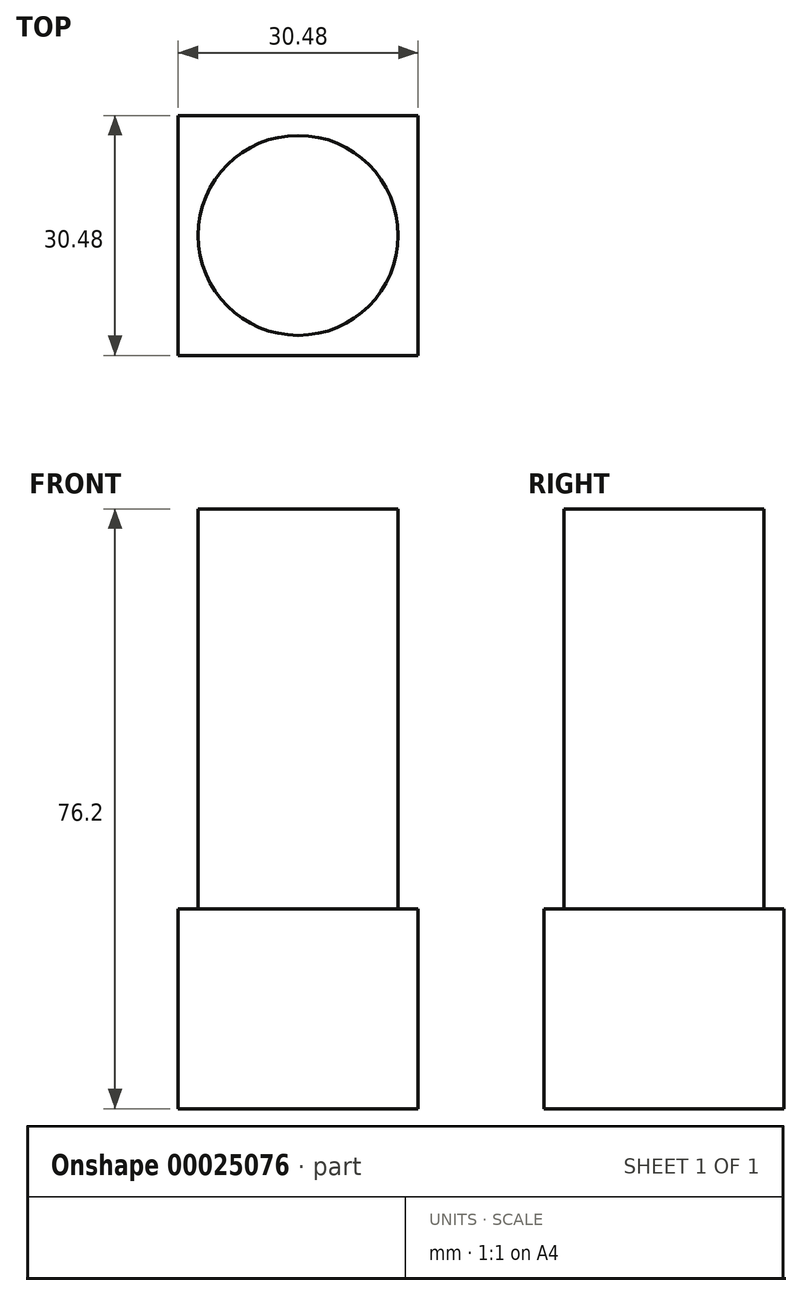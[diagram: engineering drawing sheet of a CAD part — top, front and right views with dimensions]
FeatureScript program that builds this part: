
annotation { "Feature Type Name" : "Feature", "Feature Type Description" : "" }
export const myFeature = defineFeature(function(context is Context, id is Id, definition is map)
    precondition{}
    {
        {
            var Q0;
            Q0=qCreatedBy(makeId("Top.planeOp"),FACE);
            var sketch = newSketch(context, id + "F0", { "sketchPlane" : qUnion([Q0])});
            skCircle(sketch, "E0", {"center": v(0, 0) * mm, "radius": 12.7 * mm});
            skLineSegment(sketch, "E1.bottom", {"start": v(-15.24, 15.24) * mm, "end": v(15.24, 15.24) * mm});
            skLineSegment(sketch, "E1.top", {"start": v(-15.24, -15.24) * mm, "end": v(15.24, -15.24) * mm});
            skLineSegment(sketch, "E1.left", {"start": v(-15.24, 15.24) * mm, "end": v(-15.24, -15.24) * mm});
            skLineSegment(sketch, "E1.right", {"start": v(15.24, 15.24) * mm, "end": v(15.24, -15.24) * mm});
            skSolve(sketch);
        }
        {
            var Q0;
            Q0 = qSketchRegion(id + "F0", true);
            var Q1;
            Q1=makeQuery(id+"F0.imprint","IMPRINT",FACE,{"disambiguationData":[TD([[makeQuery(id+"F0.imprint","IMPRINT",EDGE,{"derivedFrom":sQuery(id+"F0.wireOp",EDGE,"E0")}),1.0]])]});
            extrude(context, id + "F1", {"entities" : qUnion([Q0, Q1]), "depth" : 25.4 * mm});
        }
        {
            var Q0;
            Q0=makeQuery(id+"F0.imprint","IMPRINT",FACE,{"disambiguationData":[TD([[makeQuery(id+"F0.imprint","IMPRINT",EDGE,{"derivedFrom":sQuery(id+"F0.wireOp",EDGE,"E0")}),1.0]])]});
            extrude(context, id + "F2", {"entities" : qUnion([Q0]), "operationType" : NewBodyOperationType.ADD, "depth" : 76.2 * mm});
        }
    });
